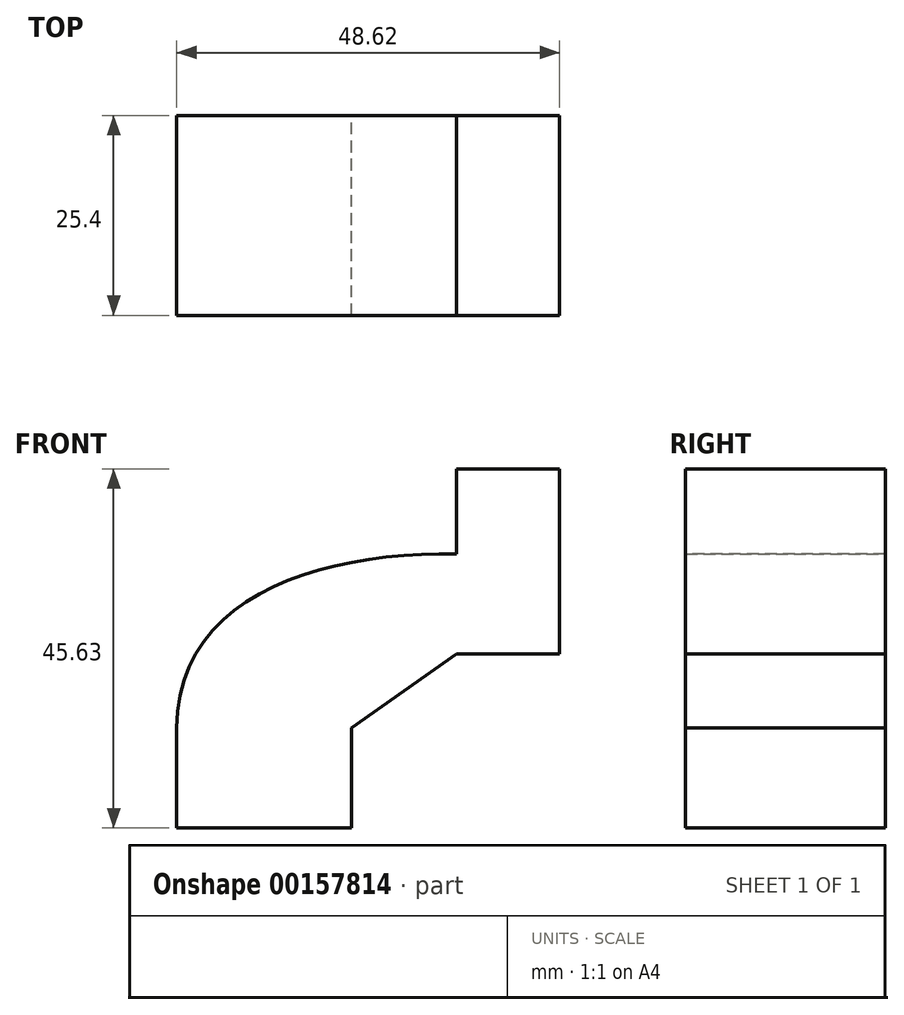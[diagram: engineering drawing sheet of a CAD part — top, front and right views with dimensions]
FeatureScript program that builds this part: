
annotation { "Feature Type Name" : "Feature", "Feature Type Description" : "" }
export const myFeature = defineFeature(function(context is Context, id is Id, definition is map)
    precondition{}
    {
        {
            var Q0;
            Q0=qCreatedBy(makeId("Front.planeOp"),FACE);
            var sketch = newSketch(context, id + "F0", { "sketchPlane" : qUnion([Q0])});
            skLineSegment(sketch, "E0.bottom", {"start": v(0, 0) * mm, "end": v(22.2, 0) * mm});
            skLineSegment(sketch, "E0.top", {"start": v(0, 12.7) * mm, "end": v(22.2, 12.7) * mm});
            skLineSegment(sketch, "E0.left", {"start": v(0, 0) * mm, "end": v(0, 12.7) * mm});
            skLineSegment(sketch, "E0.right", {"start": v(22.2, 0) * mm, "end": v(22.2, 12.7) * mm});
            skFitSpline(sketch, "E1", {"points": [v(0, 12.7) * mm, v(35.56, 34.83) * mm], "startDerivative": vector(0, 50.52) * mm, "endDerivative": vector(51.38, -0.87) * mm});
            skLineSegment(sketch, "E2", {"start": v(35.56, 34.83) * mm, "end": v(35.56, 22.13) * mm});
            skLineSegment(sketch, "E3", {"start": v(35.56, 22.13) * mm, "end": v(22.2, 12.7) * mm});
            skLineSegment(sketch, "E4.bottom", {"start": v(35.56, 34.83) * mm, "end": v(48.62, 34.83) * mm});
            skLineSegment(sketch, "E4.top", {"start": v(35.56, 22.13) * mm, "end": v(48.62, 22.13) * mm});
            skLineSegment(sketch, "E4.right", {"start": v(48.62, 34.83) * mm, "end": v(48.62, 22.13) * mm});
            skSolve(sketch);
        }
        {
            var Q0;
            Q0=makeQuery(id+"F0.imprint","IMPRINT",FACE,{"disambiguationData":[TD([[makeQuery(id+"F0.imprint","IMPRINT",EDGE,{"derivedFrom":sQuery(id+"F0.wireOp",EDGE,"E0.top")}),1.0]])]});
            var Q1;
            Q1=makeQuery(id+"F0.imprint","IMPRINT",FACE,{"disambiguationData":[TD([[makeQuery(id+"F0.imprint","IMPRINT",EDGE,{"derivedFrom":sQuery(id+"F0.wireOp",EDGE,"E0.bottom")}),1.0]])]});
            var Q2;
            Q2=makeQuery(id+"F0.imprint","IMPRINT",FACE,{"disambiguationData":[TD([[makeQuery(id+"F0.imprint","IMPRINT",EDGE,{"derivedFrom":sQuery(id+"F0.wireOp",EDGE,"E4.bottom")}),-1.0]])]});
            extrude(context, id + "F1", {"entities" : qUnion([Q0, Q1, Q2]), "endBound" : BoundingType.SYMMETRIC, "depth" : 25.4 * mm});
        }
        {
            var Q0;
            Q0=makeQuery(id+"F1.opExtrude","SWEPT_FACE",FACE,{"disambiguationData":[OSD([sQuery(id+"F0.wireOp",EDGE,"E4.bottom")])]});
            extrude(context, id + "F2", {"entities" : qUnion([Q0]), "operationType" : NewBodyOperationType.ADD, "depth" : 10.8 * mm});
        }
    });
